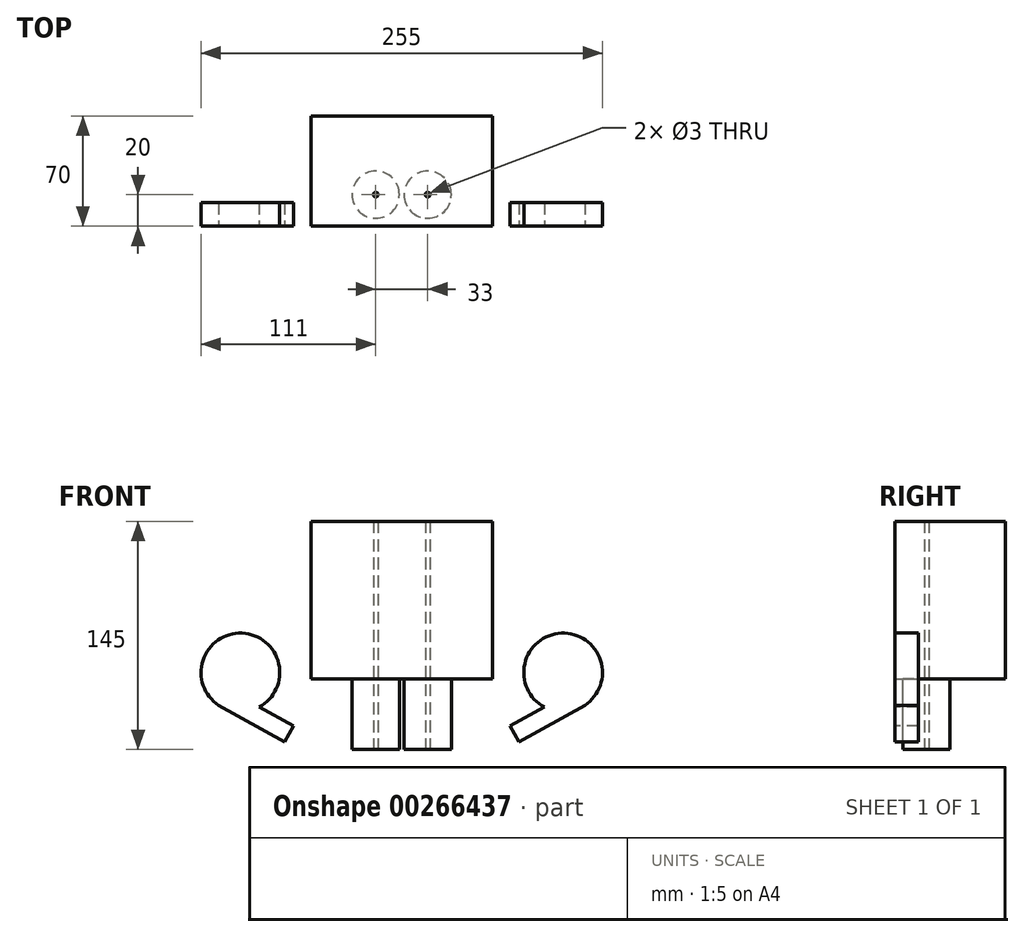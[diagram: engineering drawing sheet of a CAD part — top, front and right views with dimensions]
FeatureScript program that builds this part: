
annotation { "Feature Type Name" : "Feature", "Feature Type Description" : "" }
export const myFeature = defineFeature(function(context is Context, id is Id, definition is map)
    precondition{}
    {
        {
            var Q0;
            Q0=qCreatedBy(makeId("Front.planeOp"),FACE);
            var sketch = newSketch(context, id + "F0", { "sketchPlane" : qUnion([Q0])});
            skLineSegment(sketch, "E0.bottom", {"start": v(-57.5, 0) * mm, "end": v(57.5, 0) * mm});
            skLineSegment(sketch, "E0.top", {"start": v(-57.5, 100) * mm, "end": v(57.5, 100) * mm});
            skLineSegment(sketch, "E0.left", {"start": v(-57.5, 0) * mm, "end": v(-57.5, 100) * mm});
            skLineSegment(sketch, "E0.right", {"start": v(57.5, 0) * mm, "end": v(57.5, 100) * mm});
            skPoint(sketch, "E1", {"position": v(0, 0) * mm});
            skSolve(sketch);
        }
        {
            var Q0;
            Q0 = qSketchRegion(id + "F0", true);
            extrude(context, id + "F1", {"entities" : qUnion([Q0]), "depth" : 70 * mm});
        }
        {
            var Q0;
            Q0=makeQuery(id+"F1.opExtrude","SWEPT_FACE",FACE,{"disambiguationData":[OSD([sQuery(id+"F0.wireOp",EDGE,"E0.bottom")])]});
            var sketch = newSketch(context, id + "F2", { "sketchPlane" : qUnion([Q0])});
            skCircle(sketch, "E2", {"center": v(-16.5, 50) * mm, "radius": 15 * mm});
            skCircle(sketch, "E3", {"center": v(16.5, 50) * mm, "radius": 15 * mm});
            skSolve(sketch);
        }
        {
            var Q0;
            Q0 = qSketchRegion(id + "F2", true);
            extrude(context, id + "F3", {"entities" : qUnion([Q0]), "operationType" : NewBodyOperationType.ADD, "depth" : 45 * mm});
        }
        {
            var Q0;
            Q0=makeQuery(id+"F1.opExtrude","CAP_FACE",FACE,{"disambiguationData":[OSD([sQuery(id+"F0.wireOp",EDGE,"E0.bottom"),sQuery(id+"F0.wireOp",EDGE,"E0.top"),sQuery(id+"F0.wireOp",EDGE,"E0.left"),sQuery(id+"F0.wireOp",EDGE,"E0.right")])],"isStart":false});
            var sketch = newSketch(context, id + "F4", { "sketchPlane" : qUnion([Q0])});
            skCircle(sketch, "E4", {"center": v(-102.5, 3.97) * mm, "radius": 25 * mm});
            skLineSegment(sketch, "E5", {"start": v(-102.5, 3.97) * mm, "end": v(-55.06, -22.07) * mm, "construction": true});
            skLineSegment(sketch, "E6", {"start": v(-110.77, -6.98) * mm, "end": v(-116.26, -17) * mm});
            skLineSegment(sketch, "E7", {"start": v(-116.26, -17) * mm, "end": v(-74.37, -40) * mm});
            skLineSegment(sketch, "E8", {"start": v(-74.37, -40) * mm, "end": v(-68.87, -29.98) * mm});
            skLineSegment(sketch, "E9", {"start": v(-68.87, -29.98) * mm, "end": v(-110.77, -6.98) * mm});
            skLineSegment(sketch, "E10.MirrorCS", {"start": v(68.87, -29.98) * mm, "end": v(110.77, -6.98) * mm});
            skLineSegment(sketch, "E11.MirrorCS", {"start": v(74.37, -40) * mm, "end": v(68.87, -29.98) * mm});
            skLineSegment(sketch, "E12.MirrorCS", {"start": v(116.26, -17) * mm, "end": v(74.37, -40) * mm});
            skCircle(sketch, "E13.MirrorC", {"center": v(102.5, 3.97) * mm, "radius": 25 * mm});
            skLineSegment(sketch, "E14.MirrorCS", {"start": v(110.77, -6.98) * mm, "end": v(116.26, -17) * mm});
            skLineSegment(sketch, "E15.MirrorCS", {"start": v(102.5, 3.97) * mm, "end": v(55.06, -22.07) * mm, "construction": true});
            skSolve(sketch);
        }
        {
            var Q0;
            Q0 = qSketchRegion(id + "F4", true);
            extrude(context, id + "F5", {"entities" : qUnion([Q0]), "oppositeDirection" : true, "depth" : 15 * mm});
        }
        {
            var Q0;
            Q0=makeQuery(id+"F3.opExtrude","CAP_FACE",FACE,{"disambiguationData":[OSD([sQuery(id+"F2.wireOp",EDGE,"E2")])],"isStart":false});
            var sketch = newSketch(context, id + "F6", { "sketchPlane" : qUnion([Q0])});
            skCircle(sketch, "E16", {"center": v(-16.5, 50) * mm, "radius": 1.5 * mm});
            skCircle(sketch, "E17", {"center": v(16.5, 50) * mm, "radius": 1.5 * mm});
            skSolve(sketch);
        }
        {
            var Q0;
            Q0 = qSketchRegion(id + "F6", true);
            extrude(context, id + "F7", {"entities" : qUnion([Q0]), "operationType" : NewBodyOperationType.REMOVE, "endBound" : BoundingType.THROUGH_ALL, "oppositeDirection" : true, "depth" : 25 * mm});
        }
    });
